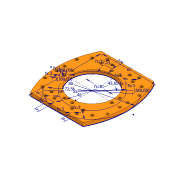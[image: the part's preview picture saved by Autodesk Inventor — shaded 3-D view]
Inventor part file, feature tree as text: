
AUTODESK INVENTOR PART (.ipt)
format: ipt  version: 2020.3 (Build 243373000, 373)  size: 182,272 bytes
history: native  units: mm
features: extrude x3, sketch x1
ambient origin geometry x8: Origin, YZ Plane, XZ Plane, XY Plane, X Axis, Y Axis, Z Axis, Center Point
bodies: Solid1 (feature_tree)
feature tree (4):
  sketch  "Sketch1"  dims[d1=81.0mm d6=7.5mm d7=5.0mm d8=30.0mm d9=3.0mm d10=7.5mm d11=5.0mm d12=3.0mm d13=3.0mm d14=5.0mm d16=4.0mm d17=0.0mm d19=48.0mm d20=55.0mm d21=3.0mm d22=4.5mm d23=3.0mm d24=4.5mm d25=40.0mm d27=360.0deg d29=10.0mm d30=0.0mm d31=80.0mm d32=72.56mm d33=3.0mm d34=3.0mm d35=20.0mm d37=360.0deg d39=45.0deg d40=3.0mm d41=200.0mm d43=360.0deg d45=10.0mm d46=0.0mm d47=3.0mm d48=3.0mm d49=3.0mm d50=3.0mm]
  extrude  "Extrusion1"  Depth=10.0mm
  extrude  "Extrusion2"  Depth=10.0mm
  extrude  "Extrusion3"  Depth=10.0mm
